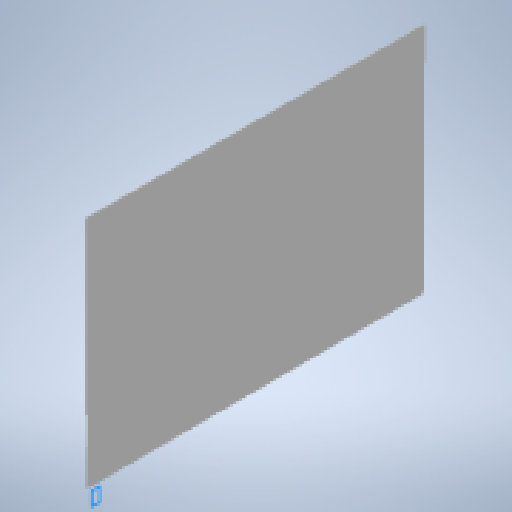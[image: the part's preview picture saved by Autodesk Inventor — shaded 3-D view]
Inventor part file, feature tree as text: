
AUTODESK INVENTOR PART (.ipt)
format: ipt  version: 2025.2 (Build 292293000, 293)  size: 449,024 bytes
history: native  units: mm
features: other x3, sketch x2, extrude x1
ambient origin geometry x8: Origin, YZ Plane, XZ Plane, XY Plane, X Axis, Y Axis, Z Axis, Center Point
bodies: Body1 (feature_tree)
feature tree (6):
  other  "ソリッド1"
  extrude  "押し出し1"  Depth=10.0mm TaperAngle=0.0deg
  other  "デカール2"
  sketch  "スケッチ1"
  sketch  "スケッチ4"
  other  "イメージ10"
